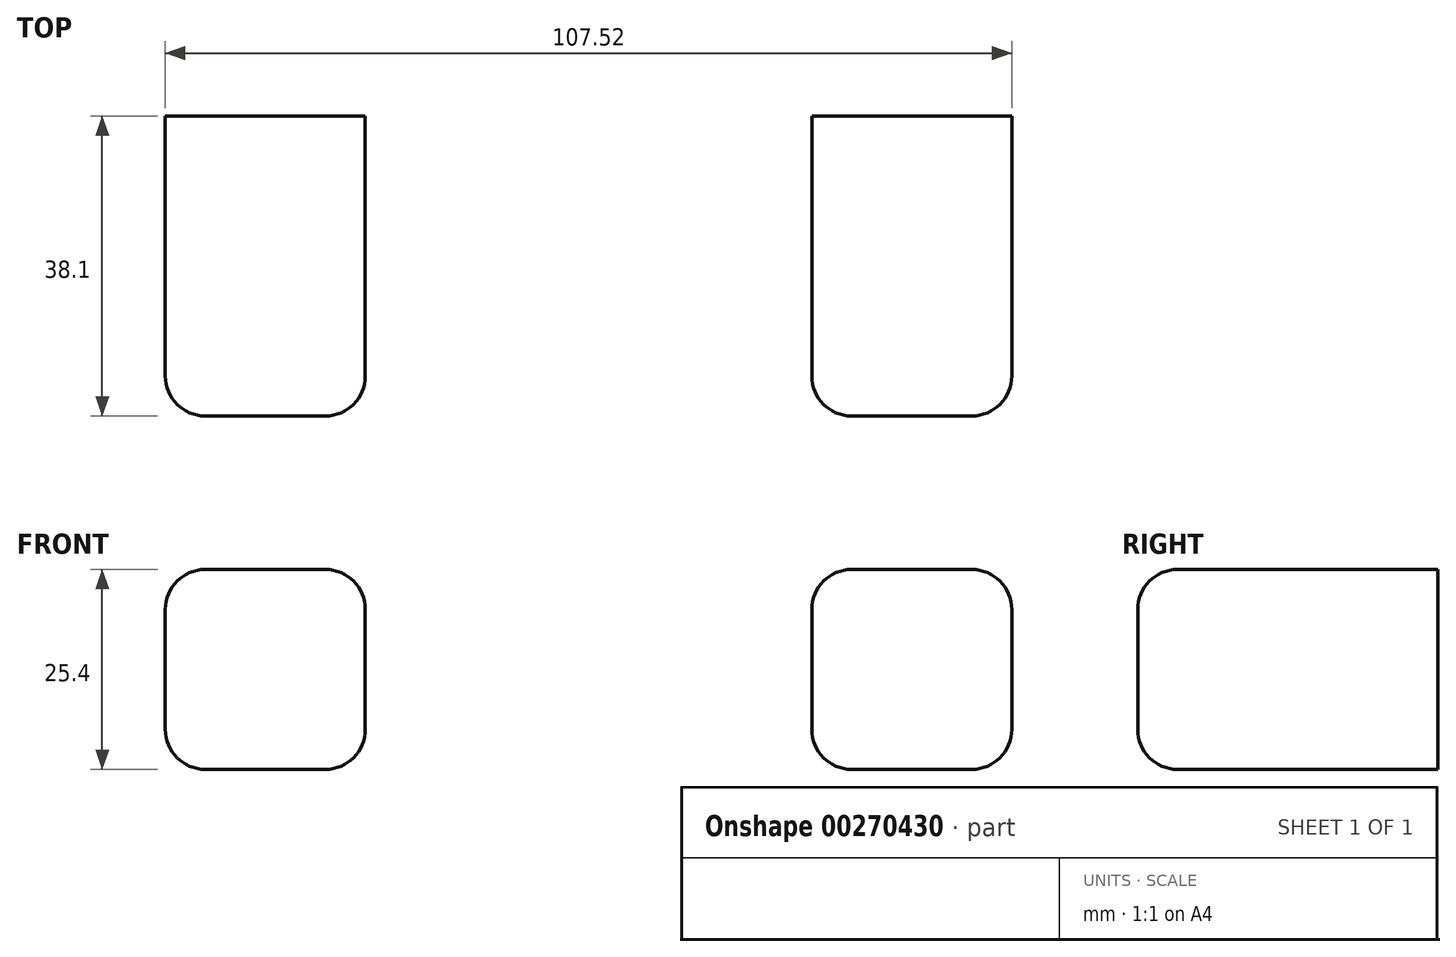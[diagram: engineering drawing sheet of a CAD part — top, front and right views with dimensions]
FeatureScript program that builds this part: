
annotation { "Feature Type Name" : "Feature", "Feature Type Description" : "" }
export const myFeature = defineFeature(function(context is Context, id is Id, definition is map)
    precondition{}
    {
        {
            var Q0;
            Q0=qCreatedBy(makeId("Front.planeOp"),FACE);
            var sketch = newSketch(context, id + "F0", { "sketchPlane" : qUnion([Q0])});
            skLineSegment(sketch, "E0.bottom", {"start": v(-28.36, 12.7) * mm, "end": v(-53.76, 12.7) * mm});
            skLineSegment(sketch, "E0.top", {"start": v(-28.36, -12.7) * mm, "end": v(-53.76, -12.7) * mm});
            skLineSegment(sketch, "E0.left", {"start": v(-28.36, 12.7) * mm, "end": v(-28.36, -12.7) * mm});
            skLineSegment(sketch, "E0.right", {"start": v(-53.76, 12.7) * mm, "end": v(-53.76, -12.7) * mm});
            skPoint(sketch, "E0.middle", {"position": v(-41.06, 0) * mm});
            skLineSegment(sketch, "E1.MirrorCS", {"start": v(28.36, 12.7) * mm, "end": v(53.76, 12.7) * mm});
            skPoint(sketch, "E2.MirrorP", {"position": v(41.06, 0) * mm});
            skLineSegment(sketch, "E3.MirrorCS", {"start": v(53.76, 12.7) * mm, "end": v(53.76, -12.7) * mm});
            skLineSegment(sketch, "E4.MirrorCS", {"start": v(28.36, 12.7) * mm, "end": v(28.36, -12.7) * mm});
            skLineSegment(sketch, "E5.MirrorCS", {"start": v(28.36, -12.7) * mm, "end": v(53.76, -12.7) * mm});
            skSolve(sketch);
        }
        {
            var Q0;
            Q0=makeQuery(id+"F0.imprint","IMPRINT",FACE,{"disambiguationData":[TD([[makeQuery(id+"F0.imprint","IMPRINT",EDGE,{"derivedFrom":sQuery(id+"F0.wireOp",EDGE,"E0.bottom")}),1.0]])]});
            var Q1;
            Q1=makeQuery(id+"F0.imprint","IMPRINT",FACE,{"disambiguationData":[TD([[makeQuery(id+"F0.imprint","IMPRINT",EDGE,{"derivedFrom":sQuery(id+"F0.wireOp",EDGE,"E1.MirrorCS")}),-1.0]])]});
            extrude(context, id + "F1", {"entities" : qUnion([Q0, Q1]), "depth" : 38.1 * mm});
        }
        {
            var Q0;
            Q0=makeQuery(id+"F1.opExtrude","CAP_EDGE",EDGE,{"disambiguationData":[OSD([sQuery(id+"F0.wireOp",EDGE,"E0.bottom")])],"isStart":false});
            var Q1;
            Q1=makeQuery(id+"F1.opExtrude","CAP_EDGE",EDGE,{"disambiguationData":[OSD([sQuery(id+"F0.wireOp",EDGE,"E0.left")])],"isStart":false});
            var Q2;
            Q2=makeQuery(id+"F1.opExtrude","CAP_EDGE",EDGE,{"disambiguationData":[OSD([sQuery(id+"F0.wireOp",EDGE,"E0.top")])],"isStart":false});
            var Q3;
            Q3=makeQuery(id+"F1.opExtrude","CAP_EDGE",EDGE,{"disambiguationData":[OSD([sQuery(id+"F0.wireOp",EDGE,"E0.right")])],"isStart":false});
            var Q4;
            Q4=makeQuery(id+"F1.opExtrude","SWEPT_EDGE",EDGE,{"disambiguationData":[OSD([sQuery(id+"F0.wireOp",EDGE,"E0.top"),sQuery(id+"F0.wireOp",EDGE,"E0.left")])]});
            var Q5;
            Q5=makeQuery(id+"F1.opExtrude","SWEPT_EDGE",EDGE,{"disambiguationData":[OSD([sQuery(id+"F0.wireOp",EDGE,"E0.top"),sQuery(id+"F0.wireOp",EDGE,"E0.right")])]});
            var Q6;
            Q6=makeQuery(id+"F1.opExtrude","SWEPT_EDGE",EDGE,{"disambiguationData":[OSD([sQuery(id+"F0.wireOp",EDGE,"E0.bottom"),sQuery(id+"F0.wireOp",EDGE,"E0.left")])]});
            var Q7;
            Q7=makeQuery(id+"F1.opExtrude","SWEPT_EDGE",EDGE,{"disambiguationData":[OSD([sQuery(id+"F0.wireOp",EDGE,"E0.bottom"),sQuery(id+"F0.wireOp",EDGE,"E0.right")])]});
            var Q8;
            Q8=makeQuery(id+"F1.opExtrude","SWEPT_EDGE",EDGE,{"disambiguationData":[OSD([sQuery(id+"F0.wireOp",EDGE,"E1.MirrorCS"),sQuery(id+"F0.wireOp",EDGE,"E3.MirrorCS")])]});
            var Q9;
            Q9=makeQuery(id+"F1.opExtrude","SWEPT_EDGE",EDGE,{"disambiguationData":[OSD([sQuery(id+"F0.wireOp",EDGE,"E1.MirrorCS"),sQuery(id+"F0.wireOp",EDGE,"E4.MirrorCS")])]});
            var Q10;
            Q10=makeQuery(id+"F1.opExtrude","SWEPT_EDGE",EDGE,{"disambiguationData":[OSD([sQuery(id+"F0.wireOp",EDGE,"E3.MirrorCS"),sQuery(id+"F0.wireOp",EDGE,"E5.MirrorCS")])]});
            var Q11;
            Q11=makeQuery(id+"F1.opExtrude","SWEPT_EDGE",EDGE,{"disambiguationData":[OSD([sQuery(id+"F0.wireOp",EDGE,"E4.MirrorCS"),sQuery(id+"F0.wireOp",EDGE,"E5.MirrorCS")])]});
            var Q12;
            Q12=makeQuery(id+"F1.opExtrude","CAP_EDGE",EDGE,{"disambiguationData":[OSD([sQuery(id+"F0.wireOp",EDGE,"E3.MirrorCS")])],"isStart":false});
            var Q13;
            Q13=makeQuery(id+"F1.opExtrude","CAP_EDGE",EDGE,{"disambiguationData":[OSD([sQuery(id+"F0.wireOp",EDGE,"E5.MirrorCS")])],"isStart":false});
            var Q14;
            Q14=makeQuery(id+"F1.opExtrude","CAP_EDGE",EDGE,{"disambiguationData":[OSD([sQuery(id+"F0.wireOp",EDGE,"E4.MirrorCS")])],"isStart":false});
            var Q15;
            Q15=makeQuery(id+"F1.opExtrude","CAP_EDGE",EDGE,{"disambiguationData":[OSD([sQuery(id+"F0.wireOp",EDGE,"E1.MirrorCS")])],"isStart":false});
            fillet(context, id + "F2", {"entities" : qUnion([Q0, Q1, Q2, Q3, Q4, Q5, Q6, Q7, Q8, Q9, Q10, Q11, Q12, Q13, Q14, Q15]), "radius" : 5.08 * mm, "tangentPropagation" : true, "allowEdgeOverflow" : false});
        }
    });
